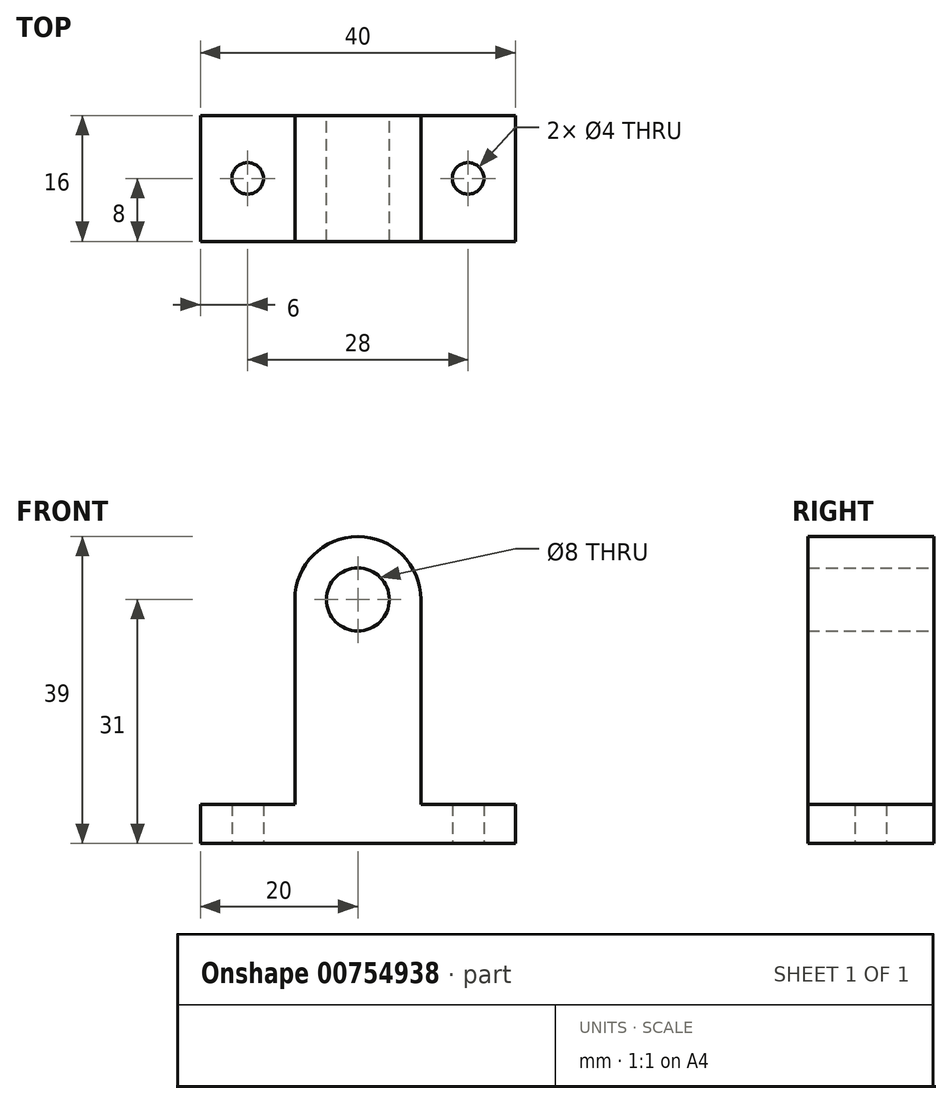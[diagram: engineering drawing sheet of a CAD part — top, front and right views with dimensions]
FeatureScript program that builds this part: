
annotation { "Feature Type Name" : "Feature", "Feature Type Description" : "" }
export const myFeature = defineFeature(function(context is Context, id is Id, definition is map)
    precondition{}
    {
        {
            var Q0;
            Q0=qCreatedBy(makeId("Front.planeOp"),FACE);
            var sketch = newSketch(context, id + "F0", { "sketchPlane" : qUnion([Q0])});
            skLineSegment(sketch, "E0.bottom", {"start": v(-20, 2.5) * mm, "end": v(-8, 2.5) * mm});
            skLineSegment(sketch, "E0.top", {"start": v(-20, -2.5) * mm, "end": v(20, -2.5) * mm});
            skLineSegment(sketch, "E0.left", {"start": v(-20, 2.5) * mm, "end": v(-20, -2.5) * mm});
            skLineSegment(sketch, "E0.right", {"start": v(20, 2.5) * mm, "end": v(20, -2.5) * mm});
            skPoint(sketch, "E0.middle", {"position": v(0, 0) * mm});
            skPoint(sketch, "E1", {"position": v(0, 28.5) * mm});
            skArc(sketch, "E2", {"start": v(8, 28.5) * mm, "mid": v(0, 36.5) * mm, "end": v(-8, 28.5) * mm});
            skLineSegment(sketch, "E3", {"start": v(8, 28.5) * mm, "end": v(8, 2.5) * mm});
            skLineSegment(sketch, "E4.0", {"start": v(-8, 28.5) * mm, "end": v(-8, 2.5) * mm});
            skLineSegment(sketch, "E5.trimOffspring", {"start": v(8, 2.5) * mm, "end": v(20, 2.5) * mm});
            skSolve(sketch);
        }
        {
            var Q0;
            Q0=makeQuery(id+"F0.imprint","IMPRINT",FACE,{"disambiguationData":[TD([[makeQuery(id+"F0.imprint","IMPRINT",EDGE,{"derivedFrom":sQuery(id+"F0.wireOp",EDGE,"E0.bottom")}),-1.0]])]});
            extrude(context, id + "F1", {"entities" : qUnion([Q0]), "depth" : 16 * mm, "offsetDistance" : 25 * mm});
        }
        {
            var Q0;
            Q0=sQuery(id+"F0.wireOp",VERTEX,"E1");
            var Q1;
            Q1=makeQuery(id+"F1.opExtrude","SWEPT_BODY",BODY,{"disambiguationData":[OSD([sQuery(id+"F0.wireOp",EDGE,"E0.bottom"),sQuery(id+"F0.wireOp",EDGE,"E0.top"),sQuery(id+"F0.wireOp",EDGE,"E0.left"),sQuery(id+"F0.wireOp",EDGE,"E0.right"),sQuery(id+"F0.wireOp",EDGE,"E2"),sQuery(id+"F0.wireOp",EDGE,"E3"),sQuery(id+"F0.wireOp",EDGE,"E4.0"),sQuery(id+"F0.wireOp",EDGE,"E5.trimOffspring")])]});
            hole(context, id + "F2", {"style" : HoleStyle.SIMPLE, "endStyle" : HoleEndStyle.THROUGH, "oppositeDirection" : true, "holeDiameter" : 8 * mm, "majorDiameter" : 5 * mm, "isTappedThrough" : true, "tappedDepth" : 8 * mm, "tapClearance" : 3, "locations" : qUnion([Q0]), "scope" : qUnion([Q1])});
        }
        {
            var Q0;
            Q0=makeQuery(id+"F1.opExtrude","SWEPT_FACE",FACE,{"disambiguationData":[OSD([sQuery(id+"F0.wireOp",EDGE,"E0.top")])]});
            var sketch = newSketch(context, id + "F3", { "sketchPlane" : qUnion([Q0])});
            skLineSegment(sketch, "E6.bottom", {"start": v(-20, 0) * mm, "end": v(20, 0) * mm});
            skLineSegment(sketch, "E6.top", {"start": v(-20, 16) * mm, "end": v(20, 16) * mm});
            skLineSegment(sketch, "E6.left", {"start": v(-20, 0) * mm, "end": v(-20, 16) * mm});
            skLineSegment(sketch, "E6.right", {"start": v(20, 0) * mm, "end": v(20, 16) * mm});
            skLineSegment(sketch, "E7.0", {"start": v(-14, 0) * mm, "end": v(-14, 16) * mm});
            skLineSegment(sketch, "E8.0", {"start": v(14, 0) * mm, "end": v(14, 16) * mm});
            skLineSegment(sketch, "E9.0", {"start": v(-20, 8) * mm, "end": v(20, 8) * mm});
            skPoint(sketch, "E10", {"position": v(-14, 8) * mm});
            skPoint(sketch, "E11", {"position": v(14, 8) * mm});
            skSolve(sketch);
        }
        {
            var Q0;
            Q0=sQuery(id+"F3.wireOp",VERTEX,"E10");
            var Q1;
            Q1=sQuery(id+"F3.wireOp",VERTEX,"E11");
            var Q2;
            Q2=makeQuery(id+"F1.opExtrude","SWEPT_BODY",BODY,{"disambiguationData":[OSD([sQuery(id+"F0.wireOp",EDGE,"E0.bottom"),sQuery(id+"F0.wireOp",EDGE,"E0.top"),sQuery(id+"F0.wireOp",EDGE,"E0.left"),sQuery(id+"F0.wireOp",EDGE,"E0.right"),sQuery(id+"F0.wireOp",EDGE,"E2"),sQuery(id+"F0.wireOp",EDGE,"E3"),sQuery(id+"F0.wireOp",EDGE,"E4.0"),sQuery(id+"F0.wireOp",EDGE,"E5.trimOffspring")])]});
            hole(context, id + "F4", {"style" : HoleStyle.SIMPLE, "endStyle" : HoleEndStyle.THROUGH, "holeDiameter" : 4 * mm, "majorDiameter" : 5 * mm, "isTappedThrough" : true, "tappedDepth" : 8 * mm, "tapClearance" : 3, "locations" : qUnion([Q0, Q1]), "scope" : qUnion([Q2])});
        }
    });
